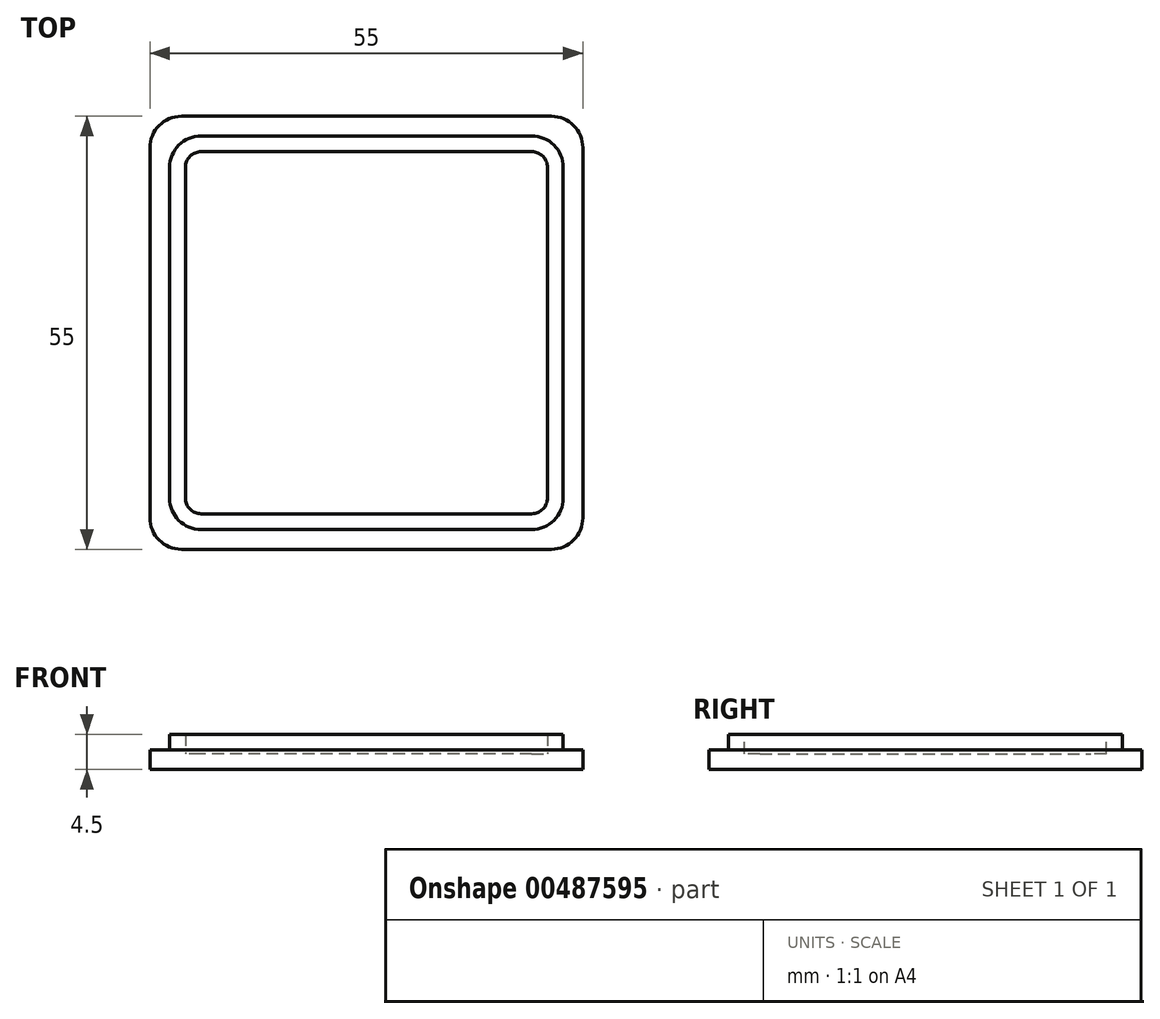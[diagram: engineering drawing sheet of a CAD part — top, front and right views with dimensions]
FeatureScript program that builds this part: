
annotation { "Feature Type Name" : "Feature", "Feature Type Description" : "" }
export const myFeature = defineFeature(function(context is Context, id is Id, definition is map)
    precondition{}
    {
        {
            assignVariable(context, id + "F0", {"name" : "shellThickness", "anyValue" : 2.5});
        }
        {
            var Q0;
            Q0=qCreatedBy(makeId("Top.planeOp"),FACE);
            var sketch = newSketch(context, id + "F1", { "sketchPlane" : qUnion([Q0])});
            skLineSegment(sketch, "E0.bottom", {"start": v(-23.5, 27.5) * mm, "end": v(23.5, 27.5) * mm});
            skLineSegment(sketch, "E0.top", {"start": v(-23.5, -27.5) * mm, "end": v(23.5, -27.5) * mm});
            skLineSegment(sketch, "E0.left", {"start": v(-27.5, 23.5) * mm, "end": v(-27.5, -23.5) * mm});
            skLineSegment(sketch, "E0.right", {"start": v(27.5, 23.5) * mm, "end": v(27.5, -23.5) * mm});
            skPoint(sketch, "E0.middle", {"position": v(0, 0) * mm});
            skPoint(sketch, "E1.visualSharp", {"position": v(-27.5, -27.5) * mm});
            skArc(sketch, "E1.filletArc", {"start": v(-27.5, -23.5) * mm, "mid": v(-26.33, -26.33) * mm, "end": v(-23.5, -27.5) * mm});
            skPoint(sketch, "E2.visualSharp", {"position": v(27.5, -27.5) * mm});
            skArc(sketch, "E2.filletArc", {"start": v(23.5, -27.5) * mm, "mid": v(26.33, -26.33) * mm, "end": v(27.5, -23.5) * mm});
            skPoint(sketch, "E3.visualSharp", {"position": v(27.5, 27.5) * mm});
            skArc(sketch, "E3.filletArc", {"start": v(27.5, 23.5) * mm, "mid": v(26.33, 26.33) * mm, "end": v(23.5, 27.5) * mm});
            skPoint(sketch, "E4.visualSharp", {"position": v(-27.5, 27.5) * mm});
            skArc(sketch, "E4.filletArc", {"start": v(-23.5, 27.5) * mm, "mid": v(-26.33, 26.33) * mm, "end": v(-27.5, 23.5) * mm});
            skSolve(sketch);
        }
        {
            var Q0;
            Q0=makeQuery(id+"F1.imprint","IMPRINT",FACE,{"disambiguationData":[TD([[makeQuery(id+"F1.imprint","IMPRINT",EDGE,{"derivedFrom":sQuery(id+"F1.wireOp",EDGE,"E0.bottom")}),-1.0]])]});
            extrude(context, id + "F2", {"entities" : qUnion([Q0]), "depth" : (getVariable(context, 'shellThickness')) * mm});
        }
        {
            var Q0;
            Q0=makeQuery(id+"F2.opExtrude","CAP_FACE",FACE,{"disambiguationData":[OSD([sQuery(id+"F1.wireOp",EDGE,"E0.bottom"),sQuery(id+"F1.wireOp",EDGE,"E0.top"),sQuery(id+"F1.wireOp",EDGE,"E0.left"),sQuery(id+"F1.wireOp",EDGE,"E0.right"),sQuery(id+"F1.wireOp",EDGE,"E1.filletArc"),sQuery(id+"F1.wireOp",EDGE,"E2.filletArc"),sQuery(id+"F1.wireOp",EDGE,"E3.filletArc"),sQuery(id+"F1.wireOp",EDGE,"E4.filletArc")])],"isStart":false});
            var sketch = newSketch(context, id + "F3", { "sketchPlane" : qUnion([Q0])});
            skLineSegment(sketch, "E5.bottom", {"start": v(-21, 25) * mm, "end": v(21, 25) * mm});
            skLineSegment(sketch, "E5.top", {"start": v(-21, -25) * mm, "end": v(21, -25) * mm});
            skLineSegment(sketch, "E5.left", {"start": v(-25, 21) * mm, "end": v(-25, -21) * mm});
            skLineSegment(sketch, "E5.right", {"start": v(25, 21) * mm, "end": v(25, -21) * mm});
            skPoint(sketch, "E5.middle", {"position": v(0, 0) * mm});
            skPoint(sketch, "E6.visualSharp", {"position": v(-25, 25) * mm});
            skArc(sketch, "E6.filletArc", {"start": v(-21, 25) * mm, "mid": v(-23.83, 23.83) * mm, "end": v(-25, 21) * mm});
            skPoint(sketch, "E7.visualSharp", {"position": v(25, 25) * mm});
            skArc(sketch, "E7.filletArc", {"start": v(25, 21) * mm, "mid": v(23.83, 23.83) * mm, "end": v(21, 25) * mm});
            skPoint(sketch, "E8.visualSharp", {"position": v(25, -25) * mm});
            skArc(sketch, "E8.filletArc", {"start": v(21, -25) * mm, "mid": v(23.83, -23.83) * mm, "end": v(25, -21) * mm});
            skPoint(sketch, "E9.visualSharp", {"position": v(-25, -25) * mm});
            skArc(sketch, "E9.filletArc", {"start": v(-25, -21) * mm, "mid": v(-23.83, -23.83) * mm, "end": v(-21, -25) * mm});
            skSolve(sketch);
        }
        {
            var Q0;
            Q0 = qSketchRegion(id + "F3", true);
            extrude(context, id + "F4", {"entities" : qUnion([Q0]), "operationType" : NewBodyOperationType.ADD, "depth" : 2 * mm});
        }
        {
            var Q0;
            Q0=makeQuery(id+"F4.opExtrude","CAP_FACE",FACE,{"disambiguationData":[OSD([sQuery(id+"F3.wireOp",EDGE,"E5.bottom"),sQuery(id+"F3.wireOp",EDGE,"E5.top"),sQuery(id+"F3.wireOp",EDGE,"E5.left"),sQuery(id+"F3.wireOp",EDGE,"E5.right"),sQuery(id+"F3.wireOp",EDGE,"E6.filletArc"),sQuery(id+"F3.wireOp",EDGE,"E7.filletArc"),sQuery(id+"F3.wireOp",EDGE,"E8.filletArc"),sQuery(id+"F3.wireOp",EDGE,"E9.filletArc")])],"isStart":false});
            shell(context, id + "F5", {"entities" : qUnion([Q0]), "thickness" : 2 * mm});
        }
    });
